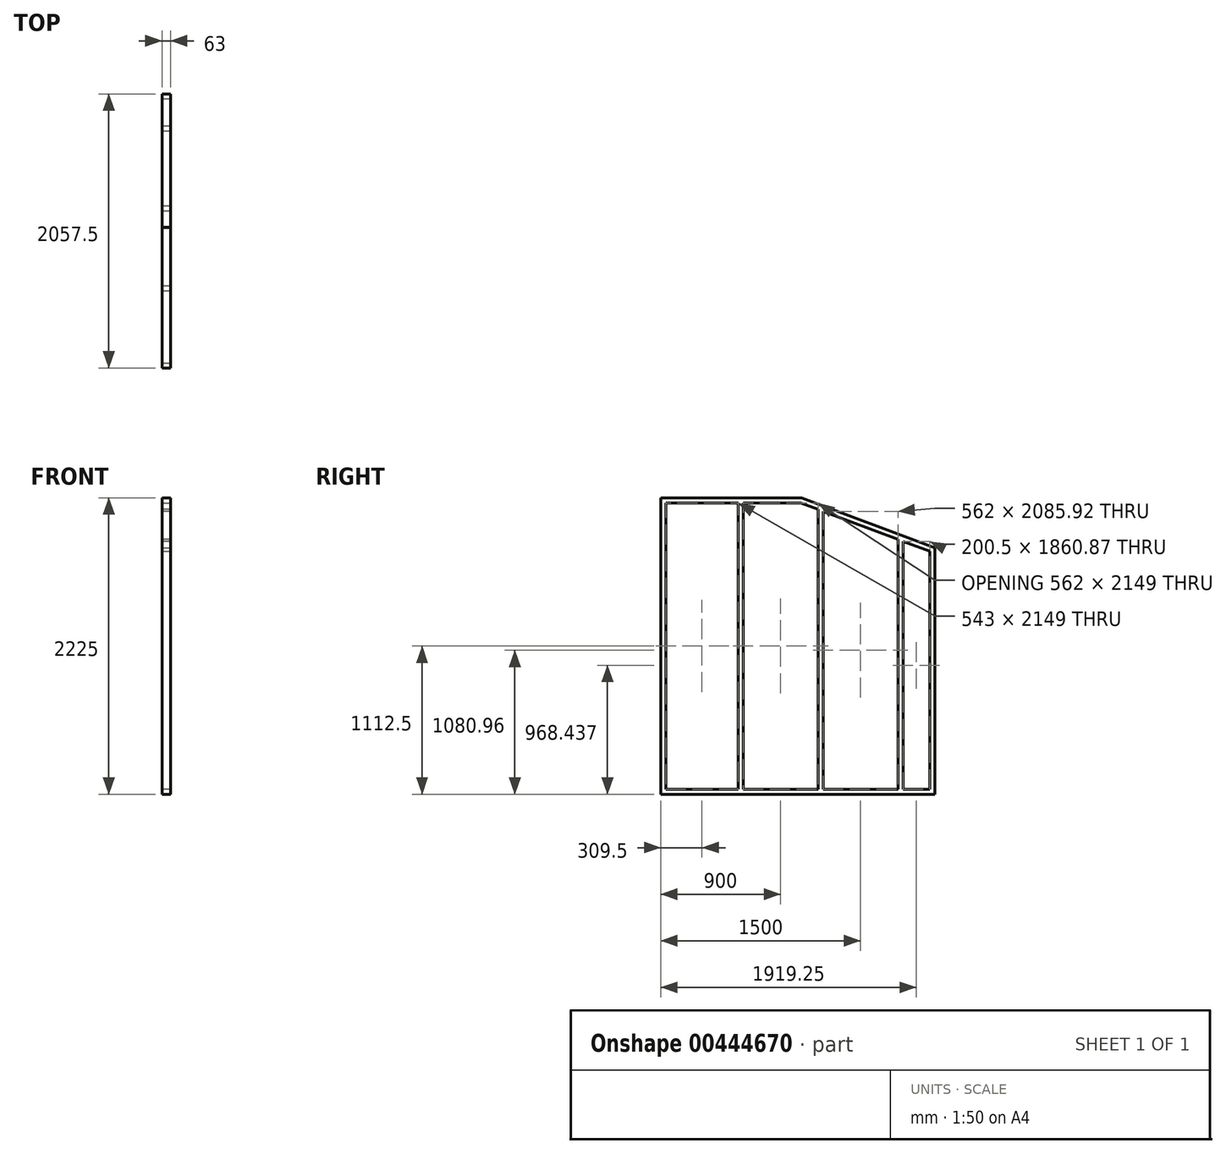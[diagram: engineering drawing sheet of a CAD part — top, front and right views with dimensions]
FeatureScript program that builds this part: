
annotation { "Feature Type Name" : "Feature", "Feature Type Description" : "" }
export const myFeature = defineFeature(function(context is Context, id is Id, definition is map)
    precondition{}
    {
        {
            var Q0;
            Q0=qCreatedBy(makeId("Top.planeOp"),FACE);
            var sketch = newSketch(context, id + "F0", { "sketchPlane" : qUnion([Q0])});
            skLineSegment(sketch, "E0.bottom", {"start": v(0, 0) * mm, "end": v(63, 0) * mm});
            skLineSegment(sketch, "E0.top", {"start": v(0, 2057.5) * mm, "end": v(63, 2057.5) * mm});
            skLineSegment(sketch, "E0.left", {"start": v(0, 0) * mm, "end": v(0, 2057.5) * mm});
            skLineSegment(sketch, "E0.right", {"start": v(63, 0) * mm, "end": v(63, 2057.5) * mm});
            skSolve(sketch);
        }
        {
            var Q0;
            Q0 = qSketchRegion(id + "F0", true);
            extrude(context, id + "F1", {"entities" : qUnion([Q0]), "depth" : 38 * mm});
        }
        {
            var Q0;
            Q0=makeQuery(id+"F1.opExtrude","CAP_FACE",FACE,{"disambiguationData":[OSD([sQuery(id+"F0.wireOp",EDGE,"E0.bottom"),sQuery(id+"F0.wireOp",EDGE,"E0.top"),sQuery(id+"F0.wireOp",EDGE,"E0.left"),sQuery(id+"F0.wireOp",EDGE,"E0.right")])],"isStart":false});
            var sketch = newSketch(context, id + "F2", { "sketchPlane" : qUnion([Q0])});
            skLineSegment(sketch, "E1.bottom", {"start": v(0, 0) * mm, "end": v(63, 0) * mm});
            skLineSegment(sketch, "E1.top", {"start": v(0, 38) * mm, "end": v(63, 38) * mm});
            skLineSegment(sketch, "E1.left", {"start": v(0, 0) * mm, "end": v(0, 38) * mm});
            skLineSegment(sketch, "E1.right", {"start": v(63, 0) * mm, "end": v(63, 38) * mm});
            skSolve(sketch);
        }
        {
            var Q0;
            Q0 = qSketchRegion(id + "F2", true);
            extrude(context, id + "F3", {"entities" : qUnion([Q0]), "operationType" : NewBodyOperationType.ADD, "depth" : 2149 * mm});
        }
        {
            var Q0;
            Q0=makeQuery(id+"F1.opExtrude","CAP_FACE",FACE,{"disambiguationData":[OSD([sQuery(id+"F0.wireOp",EDGE,"E0.bottom"),sQuery(id+"F0.wireOp",EDGE,"E0.top"),sQuery(id+"F0.wireOp",EDGE,"E0.left"),sQuery(id+"F0.wireOp",EDGE,"E0.right")])],"isStart":false});
            var sketch = newSketch(context, id + "F4", { "sketchPlane" : qUnion([Q0])});
            skLineSegment(sketch, "E2.bottom", {"start": v(0, 581) * mm, "end": v(63, 581) * mm});
            skLineSegment(sketch, "E2.top", {"start": v(0, 619) * mm, "end": v(63, 619) * mm});
            skLineSegment(sketch, "E2.left", {"start": v(0, 581) * mm, "end": v(0, 619) * mm});
            skLineSegment(sketch, "E2.right", {"start": v(63, 581) * mm, "end": v(63, 619) * mm});
            skSolve(sketch);
        }
        {
            var Q0;
            Q0=makeQuery(id+"F4.imprint","IMPRINT",FACE,{"disambiguationData":[TD([[makeQuery(id+"F4.imprint","IMPRINT",EDGE,{"derivedFrom":sQuery(id+"F4.wireOp",EDGE,"E2.bottom")}),1.0]])]});
            extrude(context, id + "F5", {"entities" : qUnion([Q0]), "operationType" : NewBodyOperationType.ADD, "depth" : 2149 * mm});
        }
        {
            var Q0;
            {var subQ0=sQuery(id+"F0.wireOp",EDGE,"E0.right");var subQ1=sQuery(id+"F0.wireOp",EDGE,"E0.left");var subQ2=sQuery(id+"F0.wireOp",EDGE,"E0.top");Q0=makeQuery(id+"F5.boolean.opBoolean","SPLIT",FACE,{"disambiguationData":[TD([makeQuery(id+"F1.opExtrude","SWEPT_FACE",FACE,{"disambiguationData":[OSD([subQ2])]})])],"derivedFrom":makeQuery(id+"F1.opExtrude","CAP_FACE",FACE,{"disambiguationData":[OSD([sQuery(id+"F0.wireOp",EDGE,"E0.bottom"),subQ2,subQ1,subQ0])],"isStart":false})});}
            var sketch = newSketch(context, id + "F6", { "sketchPlane" : qUnion([Q0])});
            skLineSegment(sketch, "E3.bottom", {"start": v(0, 1181) * mm, "end": v(63, 1181) * mm});
            skLineSegment(sketch, "E3.top", {"start": v(0, 1219) * mm, "end": v(63, 1219) * mm});
            skLineSegment(sketch, "E3.left", {"start": v(0, 1181) * mm, "end": v(0, 1219) * mm});
            skLineSegment(sketch, "E3.right", {"start": v(63, 1181) * mm, "end": v(63, 1219) * mm});
            skSolve(sketch);
        }
        {
            var Q0;
            Q0 = qSketchRegion(id + "F6", true);
            extrude(context, id + "F7", {"entities" : qUnion([Q0]), "operationType" : NewBodyOperationType.ADD, "depth" : 2149 * mm});
        }
        {
            var Q0;
            {var subQ1=sQuery(id+"F0.wireOp",EDGE,"E0.right");var subQ3=sQuery(id+"F0.wireOp",EDGE,"E0.left");var subQ5=sQuery(id+"F0.wireOp",EDGE,"E0.top");var subQ6=makeQuery(id+"F1.opExtrude","SWEPT_FACE",FACE,{"disambiguationData":[OSD([subQ5])]});Q0=makeQuery(id+"F7.boolean.opBoolean","SPLIT",FACE,{"disambiguationData":[TD([subQ6])],"derivedFrom":makeQuery(id+"F5.boolean.opBoolean","SPLIT",FACE,{"disambiguationData":[TD([subQ6])],"derivedFrom":makeQuery(id+"F1.opExtrude","CAP_FACE",FACE,{"disambiguationData":[OSD([sQuery(id+"F0.wireOp",EDGE,"E0.bottom"),subQ5,subQ3,subQ1])],"isStart":false})})});}
            var sketch = newSketch(context, id + "F8", { "sketchPlane" : qUnion([Q0])});
            skLineSegment(sketch, "E4.bottom", {"start": v(0, 1781) * mm, "end": v(63, 1781) * mm});
            skLineSegment(sketch, "E4.top", {"start": v(0, 1819) * mm, "end": v(63, 1819) * mm});
            skLineSegment(sketch, "E4.left", {"start": v(0, 1781) * mm, "end": v(0, 1819) * mm});
            skLineSegment(sketch, "E4.right", {"start": v(63, 1781) * mm, "end": v(63, 1819) * mm});
            skSolve(sketch);
        }
        {
            var Q0;
            Q0 = qSketchRegion(id + "F8", true);
            extrude(context, id + "F9", {"entities" : qUnion([Q0]), "operationType" : NewBodyOperationType.ADD, "depth" : 2149 * mm});
        }
        {
            var Q0;
            {var subQ3=sQuery(id+"F0.wireOp",EDGE,"E0.top");var subQ4=makeQuery(id+"F1.opExtrude","SWEPT_FACE",FACE,{"disambiguationData":[OSD([subQ3])]});var subQ6=sQuery(id+"F0.wireOp",EDGE,"E0.left");var subQ9=sQuery(id+"F0.wireOp",EDGE,"E0.right");Q0=makeQuery(id+"F9.boolean.opBoolean","SPLIT",FACE,{"disambiguationData":[TD([subQ4])],"derivedFrom":makeQuery(id+"F7.boolean.opBoolean","SPLIT",FACE,{"disambiguationData":[TD([subQ4])],"derivedFrom":makeQuery(id+"F5.boolean.opBoolean","SPLIT",FACE,{"disambiguationData":[TD([subQ4])],"derivedFrom":makeQuery(id+"F1.opExtrude","CAP_FACE",FACE,{"disambiguationData":[OSD([sQuery(id+"F0.wireOp",EDGE,"E0.bottom"),subQ3,subQ6,subQ9])],"isStart":false})})})});}
            var sketch = newSketch(context, id + "F10", { "sketchPlane" : qUnion([Q0])});
            skLineSegment(sketch, "E5.bottom", {"start": v(63, 2057.5) * mm, "end": v(0, 2057.5) * mm});
            skLineSegment(sketch, "E5.top", {"start": v(63, 2019.5) * mm, "end": v(0, 2019.5) * mm});
            skLineSegment(sketch, "E5.left", {"start": v(63, 2057.5) * mm, "end": v(63, 2019.5) * mm});
            skLineSegment(sketch, "E5.right", {"start": v(0, 2057.5) * mm, "end": v(0, 2019.5) * mm});
            skSolve(sketch);
        }
        {
            var Q0;
            Q0 = qSketchRegion(id + "F10", true);
            extrude(context, id + "F11", {"entities" : qUnion([Q0]), "operationType" : NewBodyOperationType.ADD, "depth" : 2149 * mm});
        }
        {
            var Q0;
            Q0=makeQuery(id+"F3.opExtrude","CAP_FACE",FACE,{"disambiguationData":[OSD([sQuery(id+"F2.wireOp",EDGE,"E1.bottom"),sQuery(id+"F2.wireOp",EDGE,"E1.top"),sQuery(id+"F2.wireOp",EDGE,"E1.left"),sQuery(id+"F2.wireOp",EDGE,"E1.right")])],"isStart":false});
            var sketch = newSketch(context, id + "F12", { "sketchPlane" : qUnion([Q0])});
            skPoint(sketch, "E6.oppositeSnap0", {"position": v(63, 19) * mm});
            skLineSegment(sketch, "E6.bottom", {"start": v(0, 0) * mm, "end": v(63, 0) * mm});
            skLineSegment(sketch, "E6.top", {"start": v(0, 1819.51) * mm, "end": v(63, 1819.51) * mm});
            skLineSegment(sketch, "E6.left", {"start": v(0, 0) * mm, "end": v(0, 1819.51) * mm});
            skLineSegment(sketch, "E6.right", {"start": v(63, 0) * mm, "end": v(63, 1819.51) * mm});
            skSolve(sketch);
        }
        {
            var Q0;
            Q0 = qSketchRegion(id + "F12", true);
            extrude(context, id + "F13", {"entities" : qUnion([Q0]), "operationType" : NewBodyOperationType.ADD, "depth" : 38 * mm});
        }
        {
            var Q0;
            Q0=makeQuery(id+"F13.boolean.opBoolean","MERGE",FACE,{"derivedFrom":[makeQuery(id+"F11.boolean.opBoolean","MERGE",FACE,{"derivedFrom":[makeQuery(id+"F9.boolean.opBoolean","MERGE",FACE,{"derivedFrom":[makeQuery(id+"F7.boolean.opBoolean","MERGE",FACE,{"derivedFrom":[makeQuery(id+"F5.boolean.opBoolean","MERGE",FACE,{"derivedFrom":[makeQuery(id+"F3.boolean.opBoolean","MERGE",FACE,{"derivedFrom":[makeQuery(id+"F1.opExtrude","SWEPT_FACE",FACE,{"disambiguationData":[OSD([sQuery(id+"F0.wireOp",EDGE,"E0.right")])]}),makeQuery(id+"F3.opExtrude","SWEPT_FACE",FACE,{"disambiguationData":[OSD([sQuery(id+"F2.wireOp",EDGE,"E1.right")])]})]}),makeQuery(id+"F5.opExtrude","SWEPT_FACE",FACE,{"disambiguationData":[OSD([sQuery(id+"F4.wireOp",EDGE,"E2.right")])]})]}),makeQuery(id+"F7.opExtrude","SWEPT_FACE",FACE,{"disambiguationData":[OSD([sQuery(id+"F6.wireOp",EDGE,"E3.right")])]})]}),makeQuery(id+"F9.opExtrude","SWEPT_FACE",FACE,{"disambiguationData":[OSD([sQuery(id+"F8.wireOp",EDGE,"E4.right")])]})]}),makeQuery(id+"F11.opExtrude","SWEPT_FACE",FACE,{"disambiguationData":[OSD([sQuery(id+"F10.wireOp",EDGE,"E5.left")])]})]}),makeQuery(id+"F13.opExtrude","SWEPT_FACE",FACE,{"disambiguationData":[OSD([sQuery(id+"F12.wireOp",EDGE,"E6.right")])]})]});
            var sketch = newSketch(context, id + "F14", { "sketchPlane" : qUnion([Q0])});
            skLineSegment(sketch, "E7", {"start": v(1057.5, 2225) * mm, "end": v(2057.5, 1850) * mm});
            skLineSegment(sketch, "E8", {"start": v(2057.5, 1850) * mm, "end": v(2057.5, 1809.42) * mm});
            skLineSegment(sketch, "E9.0", {"start": v(619, 2187) * mm, "end": v(1181, 2187) * mm});
            skLineSegment(sketch, "E10", {"start": v(1057.5, 2225) * mm, "end": v(1050.83, 2187) * mm});
            skLineSegment(sketch, "E11", {"start": v(1050.83, 2187) * mm, "end": v(2057.5, 1809.42) * mm});
            skSolve(sketch);
        }
        {
            var Q0;
            Q0 = qSketchRegion(id + "F14", true);
            extrude(context, id + "F15", {"entities" : qUnion([Q0]), "operationType" : NewBodyOperationType.ADD, "oppositeDirection" : true, "depth" : 63 * mm});
        }
        {
            var Q0;
            Q0=makeQuery(id+"F15.boolean.opBoolean","MERGE",FACE,{"derivedFrom":[makeQuery(id+"F13.boolean.opBoolean","MERGE",FACE,{"derivedFrom":[makeQuery(id+"F11.boolean.opBoolean","MERGE",FACE,{"derivedFrom":[makeQuery(id+"F9.boolean.opBoolean","MERGE",FACE,{"derivedFrom":[makeQuery(id+"F7.boolean.opBoolean","MERGE",FACE,{"derivedFrom":[makeQuery(id+"F5.boolean.opBoolean","MERGE",FACE,{"derivedFrom":[makeQuery(id+"F3.boolean.opBoolean","MERGE",FACE,{"derivedFrom":[makeQuery(id+"F1.opExtrude","SWEPT_FACE",FACE,{"disambiguationData":[OSD([sQuery(id+"F0.wireOp",EDGE,"E0.right")])]}),makeQuery(id+"F3.opExtrude","SWEPT_FACE",FACE,{"disambiguationData":[OSD([sQuery(id+"F2.wireOp",EDGE,"E1.right")])]})]}),makeQuery(id+"F5.opExtrude","SWEPT_FACE",FACE,{"disambiguationData":[OSD([sQuery(id+"F4.wireOp",EDGE,"E2.right")])]})]}),makeQuery(id+"F7.opExtrude","SWEPT_FACE",FACE,{"disambiguationData":[OSD([sQuery(id+"F6.wireOp",EDGE,"E3.right")])]})]}),makeQuery(id+"F9.opExtrude","SWEPT_FACE",FACE,{"disambiguationData":[OSD([sQuery(id+"F8.wireOp",EDGE,"E4.right")])]})]}),makeQuery(id+"F11.opExtrude","SWEPT_FACE",FACE,{"disambiguationData":[OSD([sQuery(id+"F10.wireOp",EDGE,"E5.left")])]})]}),makeQuery(id+"F13.opExtrude","SWEPT_FACE",FACE,{"disambiguationData":[OSD([sQuery(id+"F12.wireOp",EDGE,"E6.right")])]})]}),makeQuery(id+"F15.opExtrude","CAP_FACE",FACE,{"disambiguationData":[OSD([sQuery(id+"F14.wireOp",EDGE,"E7"),sQuery(id+"F14.wireOp",EDGE,"E8"),sQuery(id+"F14.wireOp",EDGE,"E10"),sQuery(id+"F14.wireOp",EDGE,"E11")])],"isStart":true})]});
            var sketch = newSketch(context, id + "F16", { "sketchPlane" : qUnion([Q0])});
            skLineSegment(sketch, "E12", {"start": v(1781, 1953.69) * mm, "end": v(958.91, 2261.97) * mm});
            skLineSegment(sketch, "E13", {"start": v(1781, 1953.69) * mm, "end": v(2119.42, 1826.78) * mm});
            skLineSegment(sketch, "E14", {"start": v(2057.5, 1850) * mm, "end": v(2057.5, 2225) * mm});
            skLineSegment(sketch, "E15", {"start": v(2057.5, 2225) * mm, "end": v(1057.5, 2225) * mm});
            skSolve(sketch);
        }
        {
            var Q0;
            {var subQ2=sQuery(id+"F12.wireOp",EDGE,"E6.right");var subQ8=sQuery(id+"F12.wireOp",EDGE,"E6.top");var subQ25=makeQuery(id+"F13.opExtrude","SWEPT_EDGE",EDGE,{"disambiguationData":[OSD([subQ8,subQ2])]});Q0=makeQuery(id+"F16.imprint","IMPRINT",FACE,{"disambiguationData":[TD([[makeQuery(id+"F16.imprint","IMPRINT",EDGE,{"derivedFrom":subQ25}),-1.0]])]});}
            var Q1;
            {var subQ4=sQuery(id+"F10.wireOp",EDGE,"E5.left");var subQ9=makeQuery(id+"F11.opExtrude","CAP_EDGE",EDGE,{"disambiguationData":[OSD([subQ4])],"isStart":false});Q1=makeQuery(id+"F16.imprint","IMPRINT",FACE,{"disambiguationData":[TD([[makeQuery(id+"F16.imprint","IMPRINT",EDGE,{"derivedFrom":subQ9}),-1.0]])]});}
            extrude(context, id + "F17", {"entities" : qUnion([Q0, Q1]), "operationType" : NewBodyOperationType.REMOVE, "oppositeDirection" : true, "depth" : 63 * mm});
        }
    });
